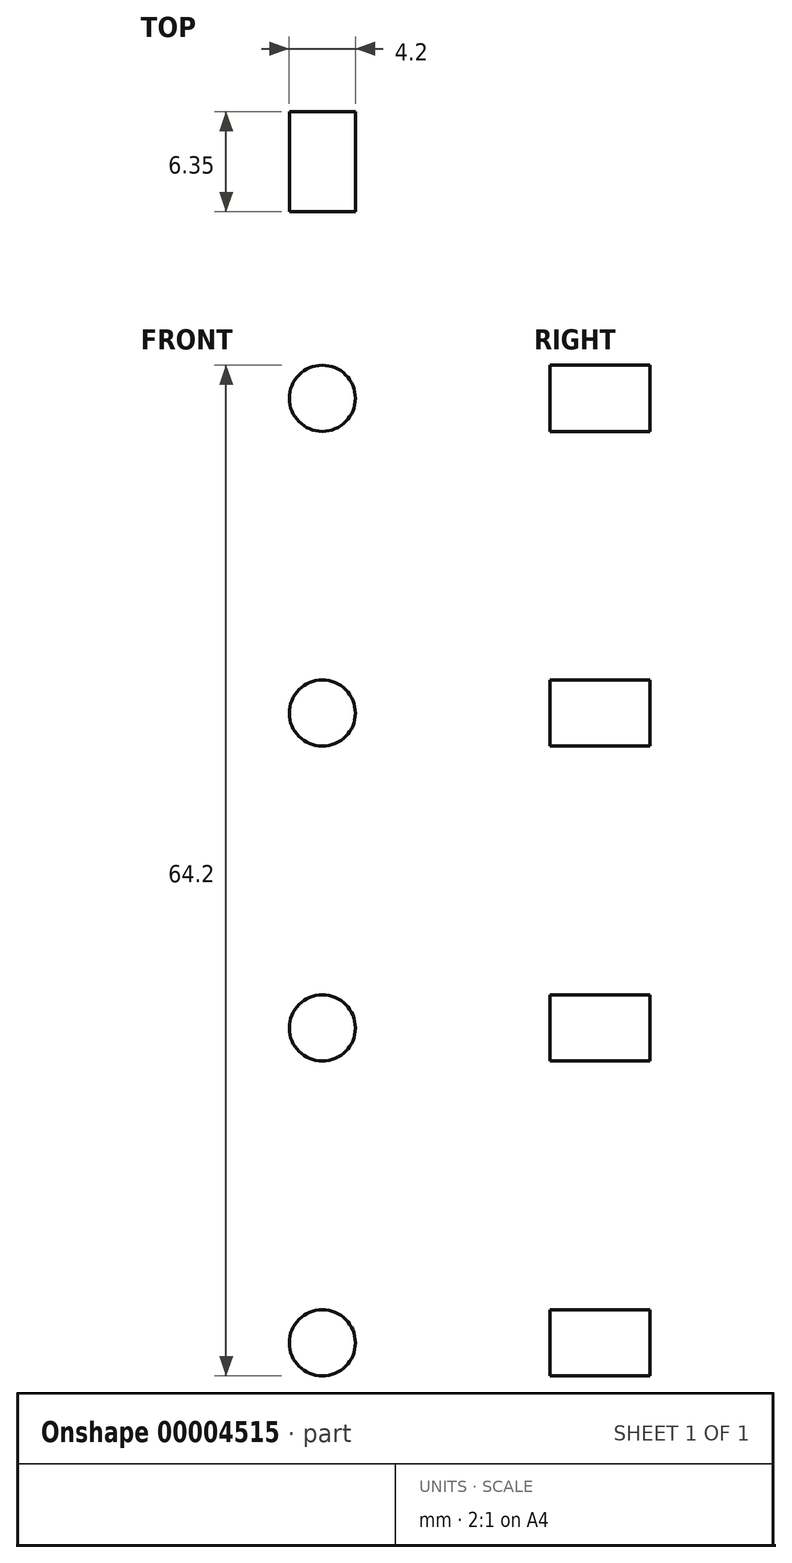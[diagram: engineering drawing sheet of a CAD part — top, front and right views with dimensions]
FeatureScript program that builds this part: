
annotation { "Feature Type Name" : "Feature", "Feature Type Description" : "" }
export const myFeature = defineFeature(function(context is Context, id is Id, definition is map)
    precondition{}
    {
        {
            var Q0;
            Q0=qCreatedBy(makeId("Front.planeOp"),FACE);
            var sketch = newSketch(context, id + "F0", { "sketchPlane" : qUnion([Q0])});
            skLineSegment(sketch, "E0.bottom", {"start": v(-157.3, -79.28) * mm, "end": v(-77.3, -79.28) * mm});
            skLineSegment(sketch, "E0.top", {"start": v(-157.3, 20.72) * mm, "end": v(292.7, 20.72) * mm});
            skLineSegment(sketch, "E0.left", {"start": v(-157.3, -79.28) * mm, "end": v(-157.3, 20.72) * mm});
            skLineSegment(sketch, "E0.right", {"start": v(292.7, -79.28) * mm, "end": v(292.7, 20.72) * mm});
            skLineSegment(sketch, "E1", {"start": v(212.7, -79.28) * mm, "end": v(292.7, -79.28) * mm});
            skLineSegment(sketch, "E2", {"start": v(-77.3, -79.28) * mm, "end": v(-77.3, -59.28) * mm});
            skLineSegment(sketch, "E3", {"start": v(-77.3, -59.28) * mm, "end": v(212.7, -59.28) * mm});
            skLineSegment(sketch, "E4", {"start": v(212.7, -59.28) * mm, "end": v(212.7, -79.28) * mm});
            skLineSegment(sketch, "E5", {"start": v(-157.3, -29.28) * mm, "end": v(292.7, -29.28) * mm, "construction": true});
            skLineSegment(sketch, "E6", {"start": v(-147.3, 20.72) * mm, "end": v(-147.3, -79.28) * mm, "construction": true});
            skLineSegment(sketch, "E7", {"start": v(-157.3, -29.28) * mm, "end": v(-147.3, -29.28) * mm, "construction": true});
            skSolve(sketch);
        }
        {
            var Q0;
            Q0=makeQuery(id+"F0.imprint","IMPRINT",FACE,{"disambiguationData":[TD([[makeQuery(id+"F0.imprint","IMPRINT",EDGE,{"derivedFrom":sQuery(id+"F0.wireOp",EDGE,"E0.top")}),-1.0]])]});
            extrude(context, id + "F1", {"entities" : qUnion([Q0]), "depth" : 6.35 * mm});
        }
        {
            var Q0;
            Q0=makeQuery(id+"F1.opExtrude","SWEPT_EDGE",EDGE,{"disambiguationData":[OSD([sQuery(id+"F0.wireOp",EDGE,"E0.top"),sQuery(id+"F0.wireOp",EDGE,"E0.right")])]});
            var Q1;
            Q1=makeQuery(id+"F1.opExtrude","SWEPT_EDGE",EDGE,{"disambiguationData":[OSD([sQuery(id+"F0.wireOp",EDGE,"E0.right"),sQuery(id+"F0.wireOp",EDGE,"E1")])]});
            var Q2;
            Q2=makeQuery(id+"F1.opExtrude","SWEPT_EDGE",EDGE,{"disambiguationData":[OSD([sQuery(id+"F0.wireOp",EDGE,"E0.bottom"),sQuery(id+"F0.wireOp",EDGE,"E2")])]});
            var Q3;
            Q3=makeQuery(id+"F1.opExtrude","SWEPT_EDGE",EDGE,{"disambiguationData":[OSD([sQuery(id+"F0.wireOp",EDGE,"E3"),sQuery(id+"F0.wireOp",EDGE,"E4")])]});
            var Q4;
            Q4=makeQuery(id+"F1.opExtrude","SWEPT_EDGE",EDGE,{"disambiguationData":[OSD([sQuery(id+"F0.wireOp",EDGE,"E2"),sQuery(id+"F0.wireOp",EDGE,"E3")])]});
            var Q5;
            Q5=makeQuery(id+"F1.opExtrude","SWEPT_EDGE",EDGE,{"disambiguationData":[OSD([sQuery(id+"F0.wireOp",EDGE,"E0.left"),sQuery(id+"F0.wireOp",EDGE,"E0.bottom")])]});
            var Q6;
            Q6=makeQuery(id+"F1.opExtrude","SWEPT_EDGE",EDGE,{"disambiguationData":[OSD([sQuery(id+"F0.wireOp",EDGE,"E0.top"),sQuery(id+"F0.wireOp",EDGE,"E0.left")])]});
            var Q7;
            Q7=makeQuery(id+"F1.opExtrude","SWEPT_EDGE",EDGE,{"disambiguationData":[OSD([sQuery(id+"F0.wireOp",EDGE,"E4"),sQuery(id+"F0.wireOp",EDGE,"E1")])]});
            fillet(context, id + "F2", {"entities" : qUnion([Q0, Q1, Q2, Q3, Q4, Q5, Q6, Q7]), "radius" : 7 * mm, "tangentPropagation" : true, "allowEdgeOverflow" : false});
        }
        {
            var Q0;
            Q0=makeQuery(id+"F1.opExtrude","CAP_FACE",FACE,{"disambiguationData":[OSD([sQuery(id+"F0.wireOp",EDGE,"E0.top"),sQuery(id+"F0.wireOp",EDGE,"E0.left"),sQuery(id+"F0.wireOp",EDGE,"E0.right"),sQuery(id+"F0.wireOp",EDGE,"E0.bottom"),sQuery(id+"F0.wireOp",EDGE,"E2"),sQuery(id+"F0.wireOp",EDGE,"E3"),sQuery(id+"F0.wireOp",EDGE,"E4"),sQuery(id+"F0.wireOp",EDGE,"E1")])],"isStart":false});
            var sketch = newSketch(context, id + "F3", { "sketchPlane" : qUnion([Q0])});
            skLineSegment(sketch, "E8", {"start": v(-157.3, -29.28) * mm, "end": v(-147.3, -29.28) * mm, "construction": true});
            skLineSegment(sketch, "E9", {"start": v(-147.3, 20.72) * mm, "end": v(-147.3, -79.28) * mm, "construction": true});
            skCircle(sketch, "E10", {"center": v(-147.3, -19.28) * mm, "radius": 2.1 * mm});
            skCircle(sketch, "E11", {"center": v(-147.3, -39.28) * mm, "radius": 2.1 * mm});
            skCircle(sketch, "E12", {"center": v(-147.3, 0.72) * mm, "radius": 2.1 * mm});
            skCircle(sketch, "E13", {"center": v(-147.3, -59.28) * mm, "radius": 2.1 * mm});
            skLineSegment(sketch, "E14", {"start": v(67.7, -59.28) * mm, "end": v(67.7, 20.72) * mm, "construction": true});
            skCircle(sketch, "E15.0.MirrorC", {"center": v(282.7, -59.28) * mm, "radius": 2.1 * mm});
            skCircle(sketch, "E15.1.MirrorC", {"center": v(282.7, -39.28) * mm, "radius": 2.1 * mm});
            skCircle(sketch, "E15.2.MirrorC", {"center": v(282.7, -19.28) * mm, "radius": 2.1 * mm});
            skCircle(sketch, "E15.3.MirrorC", {"center": v(282.7, 0.72) * mm, "radius": 2.1 * mm});
            skSolve(sketch);
        }
        {
            var Q0;
            Q0=makeQuery(id+"F3.imprint","IMPRINT",FACE,{"disambiguationData":[TD([[makeQuery(id+"F3.imprint","IMPRINT",EDGE,{"derivedFrom":sQuery(id+"F3.wireOp",EDGE,"E12")}),1.0]])]});
            var Q1;
            Q1=makeQuery(id+"F3.imprint","IMPRINT",FACE,{"disambiguationData":[TD([[makeQuery(id+"F3.imprint","IMPRINT",EDGE,{"derivedFrom":sQuery(id+"F3.wireOp",EDGE,"E10")}),1.0]])]});
            var Q2;
            Q2=makeQuery(id+"F3.imprint","IMPRINT",FACE,{"disambiguationData":[TD([[makeQuery(id+"F3.imprint","IMPRINT",EDGE,{"derivedFrom":sQuery(id+"F3.wireOp",EDGE,"E11")}),1.0]])]});
            var Q3;
            Q3=makeQuery(id+"F3.imprint","IMPRINT",FACE,{"disambiguationData":[TD([[makeQuery(id+"F3.imprint","IMPRINT",EDGE,{"derivedFrom":sQuery(id+"F3.wireOp",EDGE,"E13")}),1.0]])]});
            var Q4;
            Q4=makeQuery(id+"F3.imprint","IMPRINT",FACE,{"disambiguationData":[TD([[makeQuery(id+"F3.imprint","IMPRINT",EDGE,{"derivedFrom":sQuery(id+"F3.wireOp",EDGE,"E15.1.MirrorC")}),-1.0]])]});
            var Q5;
            Q5=makeQuery(id+"F3.imprint","IMPRINT",FACE,{"disambiguationData":[TD([[makeQuery(id+"F3.imprint","IMPRINT",EDGE,{"derivedFrom":sQuery(id+"F3.wireOp",EDGE,"E15.2.MirrorC")}),-1.0]])]});
            var Q6;
            Q6=makeQuery(id+"F3.imprint","IMPRINT",FACE,{"disambiguationData":[TD([[makeQuery(id+"F3.imprint","IMPRINT",EDGE,{"derivedFrom":sQuery(id+"F3.wireOp",EDGE,"E15.0.MirrorC")}),-1.0]])]});
            var Q7;
            Q7=makeQuery(id+"F3.imprint","IMPRINT",FACE,{"disambiguationData":[TD([[makeQuery(id+"F3.imprint","IMPRINT",EDGE,{"derivedFrom":sQuery(id+"F3.wireOp",EDGE,"E15.3.MirrorC")}),-1.0]])]});
            var Q8;
            Q8=makeQuery(id+"F1.opExtrude","CAP_FACE",FACE,{"disambiguationData":[OSD([sQuery(id+"F0.wireOp",EDGE,"E0.top"),sQuery(id+"F0.wireOp",EDGE,"E0.left"),sQuery(id+"F0.wireOp",EDGE,"E0.right"),sQuery(id+"F0.wireOp",EDGE,"E0.bottom"),sQuery(id+"F0.wireOp",EDGE,"E2"),sQuery(id+"F0.wireOp",EDGE,"E3"),sQuery(id+"F0.wireOp",EDGE,"E4"),sQuery(id+"F0.wireOp",EDGE,"E1")])],"isStart":true});
            extrude(context, id + "F4", {"entities" : qUnion([Q0, Q1, Q2, Q3, Q4, Q5, Q6, Q7]), "operationType" : NewBodyOperationType.REMOVE, "endBound" : BoundingType.UP_TO_SURFACE, "oppositeDirection" : true, "endBoundEntityFace" : qUnion([Q8]), "depth" : 25 * mm});
        }
    });
